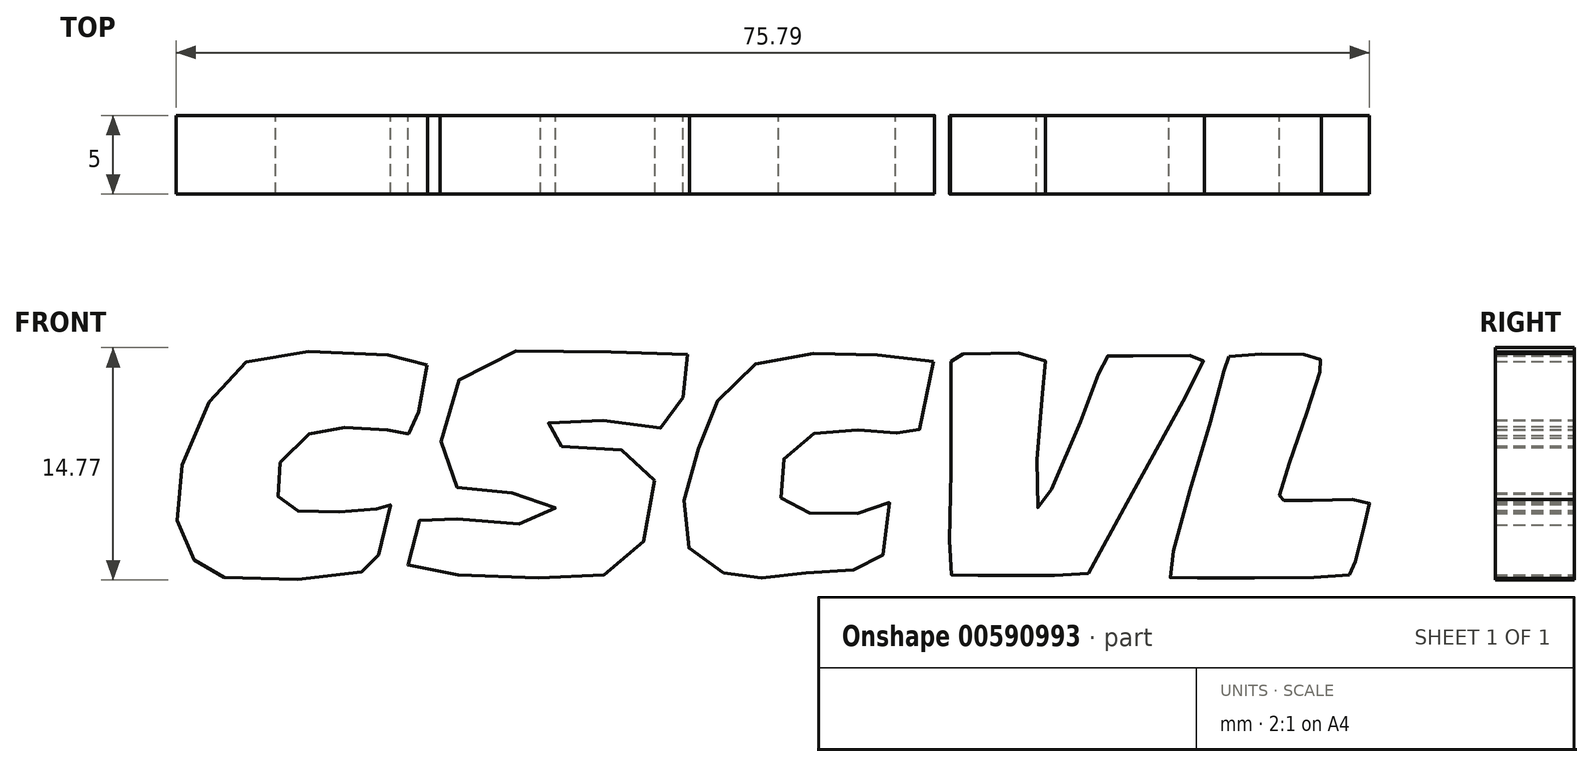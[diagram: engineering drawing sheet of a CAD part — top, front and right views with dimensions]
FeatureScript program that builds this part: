
annotation { "Feature Type Name" : "Feature", "Feature Type Description" : "" }
export const myFeature = defineFeature(function(context is Context, id is Id, definition is map)
    precondition{}
    {
        {
            var Q0;
            Q0=qCreatedBy(makeId("Front.planeOp"),FACE);
            var sketch = newSketch(context, id + "F0", { "sketchPlane" : qUnion([Q0])});
            skFitSpline(sketch, "E0", {"points": [v(-69.87, 20.81) * mm, v(-71.56, 21.4) * mm, v(-79.64, 21.54) * mm, v(-82.92, 19.67) * mm, v(-85.57, 13.97) * mm, v(-85.57, 10.14) * mm, v(-84.43, 8.13) * mm, v(-82.88, 7.35) * mm, v(-75.26, 7.45) * mm, v(-73.34, 7.95) * mm, v(-73.16, 8.22) * mm, v(-72.2, 11.92) * mm, v(-72.34, 11.96) * mm, v(-72.89, 12) * mm, v(-73.07, 11.69) * mm, v(-73.52, 11.55) * mm, v(-77.27, 11.46) * mm, v(-78.27, 11.6) * mm, v(-79.09, 12.05) * mm, v(-79.5, 13.15) * mm, v(-79, 15.02) * mm, v(-77.22, 16.52) * mm, v(-75.49, 16.84) * mm, v(-72.7, 16.8) * mm, v(-71.6, 16.39) * mm, v(-71.29, 16.39) * mm, v(-70.6, 16.7) * mm, v(-70.47, 17.66) * mm, v(-69.87, 20.81) * mm]});
            skFitSpline(sketch, "E1", {"points": [v(-53.35, 21.48) * mm, v(-55.95, 21.53) * mm, v(-60.62, 21.91) * mm, v(-65.39, 21.48) * mm, v(-67.29, 20.5) * mm, v(-68.48, 18.82) * mm, v(-68.97, 16.38) * mm, v(-68.97, 14.53) * mm, v(-68.26, 13.4) * mm, v(-67.56, 12.74) * mm, v(-65.88, 12.69) * mm, v(-63.27, 12.63) * mm, v(-61.97, 12.36) * mm, v(-61.75, 11.66) * mm, v(-62.24, 11.17) * mm, v(-62.79, 10.74) * mm, v(-65.06, 10.84) * mm, v(-67.07, 11) * mm, v(-68.75, 11.17) * mm, v(-69.46, 11.44) * mm, v(-70.27, 11.12) * mm, v(-70.43, 10.25) * mm, v(-70.7, 9) * mm, v(-71.09, 7.97) * mm, v(-70.1, 7.64) * mm, v(-67.83, 7.48) * mm, v(-63.82, 7.32) * mm, v(-61.48, 7.32) * mm, v(-58.88, 7.48) * mm, v(-57.52, 7.75) * mm, v(-56.33, 9.27) * mm, v(-55.52, 11.06) * mm, v(-55.46, 13.56) * mm, v(-55.84, 14.86) * mm, v(-57.14, 15.4) * mm, v(-59.15, 15.5) * mm, v(-61.16, 15.67) * mm, v(-62.46, 15.67) * mm, v(-62.62, 16.6) * mm, v(-61.92, 17.25) * mm, v(-60.18, 17.3) * mm, v(-58.28, 17.3) * mm, v(-56, 17.14) * mm, v(-54.87, 16.76) * mm, v(-54.1, 16.92) * mm, v(-53.73, 18.11) * mm, v(-53.45, 19.85) * mm, v(-53.3, 20.56) * mm, v(-53.35, 21.48) * mm]});
            skFitSpline(sketch, "E2", {"points": [v(-37.72, 21.04) * mm, v(-40.27, 21.48) * mm, v(-43.97, 21.48) * mm, v(-47.5, 21.48) * mm, v(-50, 20.21) * mm, v(-51.55, 18.37) * mm, v(-52.36, 16.37) * mm, v(-53.35, 13.44) * mm, v(-53.62, 11.53) * mm, v(-53.35, 9.4) * mm, v(-52.2, 8.05) * mm, v(-50.59, 7.53) * mm, v(-49.07, 7.3) * mm, v(-48.3, 7.3) * mm, v(-46.07, 7.57) * mm, v(-45.33, 7.66) * mm, v(-42.65, 7.82) * mm, v(-41.33, 8.18) * mm, v(-41.04, 8.53) * mm, v(-40.2, 11.8) * mm, v(-40.81, 12.05) * mm, v(-41.33, 11.57) * mm, v(-43.36, 11.44) * mm, v(-45.3, 11.44) * mm, v(-46.65, 11.57) * mm, v(-47.3, 12.11) * mm, v(-47.55, 13.37) * mm, v(-47.26, 14.8) * mm, v(-46.23, 15.92) * mm, v(-45.17, 16.53) * mm, v(-43.52, 16.73) * mm, v(-41.46, 16.7) * mm, v(-40.3, 16.63) * mm, v(-39.62, 16.21) * mm, v(-38.85, 16.34) * mm, v(-38.59, 16.82) * mm, v(-38.43, 17.95) * mm, v(-38.17, 18.95) * mm, v(-37.9, 19.82) * mm, v(-37.72, 21.04) * mm]});
            skFitSpline(sketch, "E3", {"points": [v(-36.6, 21.04) * mm, v(-36.6, 15.4) * mm, v(-36.65, 7.75) * mm, v(-36.54, 7.43) * mm, v(-36.15, 7.43) * mm, v(-28.07, 7.43) * mm, v(-27.91, 7.55) * mm, v(-20.51, 21.04) * mm, v(-20.54, 21.04) * mm, v(-20.76, 21.48) * mm, v(-21.01, 21.48) * mm, v(-26.21, 21.48) * mm, v(-26.58, 21.48) * mm, v(-27.04, 20.82) * mm, v(-27.5, 19.5) * mm, v(-30.85, 11.74) * mm, v(-31.04, 11.6) * mm, v(-31.04, 16.65) * mm, v(-30.6, 21.04) * mm, v(-31.04, 21.48) * mm, v(-36.24, 21.48) * mm, v(-36.51, 21.35) * mm, v(-36.6, 21.04) * mm]});
            skFitSpline(sketch, "E4", {"points": [v(-18.97, 21.36) * mm, v(-13.49, 21.4) * mm, v(-13.13, 21.12) * mm, v(-13.18, 20.44) * mm, v(-15.73, 12.63) * mm, v(-15.72, 12.32) * mm, v(-15.12, 12.2) * mm, v(-10.2, 12.2) * mm, v(-10.08, 11.81) * mm, v(-11.04, 7.86) * mm, v(-11.45, 7.45) * mm, v(-22.12, 7.27) * mm, v(-22.76, 7.64) * mm, v(-19.22, 20.8) * mm, v(-18.97, 21.36) * mm]});
            skSolve(sketch);
        }
        {
            var Q0;
            Q0=makeQuery(id+"F0.imprint","IMPRINT",FACE,{"disambiguationData":[TD([[makeQuery(id+"F0.imprint","IMPRINT",EDGE,{"derivedFrom":sQuery(id+"F0.wireOp",EDGE,"E4")}),-1.0]])]});
            var Q1;
            Q1=makeQuery(id+"F0.imprint","IMPRINT",FACE,{"disambiguationData":[TD([[makeQuery(id+"F0.imprint","IMPRINT",EDGE,{"derivedFrom":sQuery(id+"F0.wireOp",EDGE,"E3")}),1.0]])]});
            var Q2;
            Q2=makeQuery(id+"F0.imprint","IMPRINT",FACE,{"disambiguationData":[TD([[makeQuery(id+"F0.imprint","IMPRINT",EDGE,{"derivedFrom":sQuery(id+"F0.wireOp",EDGE,"E2")}),1.0]])]});
            var Q3;
            Q3=makeQuery(id+"F0.imprint","IMPRINT",FACE,{"disambiguationData":[TD([[makeQuery(id+"F0.imprint","IMPRINT",EDGE,{"derivedFrom":sQuery(id+"F0.wireOp",EDGE,"E1")}),1.0]])]});
            var Q4;
            Q4=makeQuery(id+"F0.imprint","IMPRINT",FACE,{"disambiguationData":[TD([[makeQuery(id+"F0.imprint","IMPRINT",EDGE,{"derivedFrom":sQuery(id+"F0.wireOp",EDGE,"E0")}),1.0]])]});
            extrude(context, id + "F1", {"entities" : qUnion([Q0, Q1, Q2, Q3, Q4]), "depth" : 5 * mm, "offsetDistance" : 25 * mm});
        }
    });
